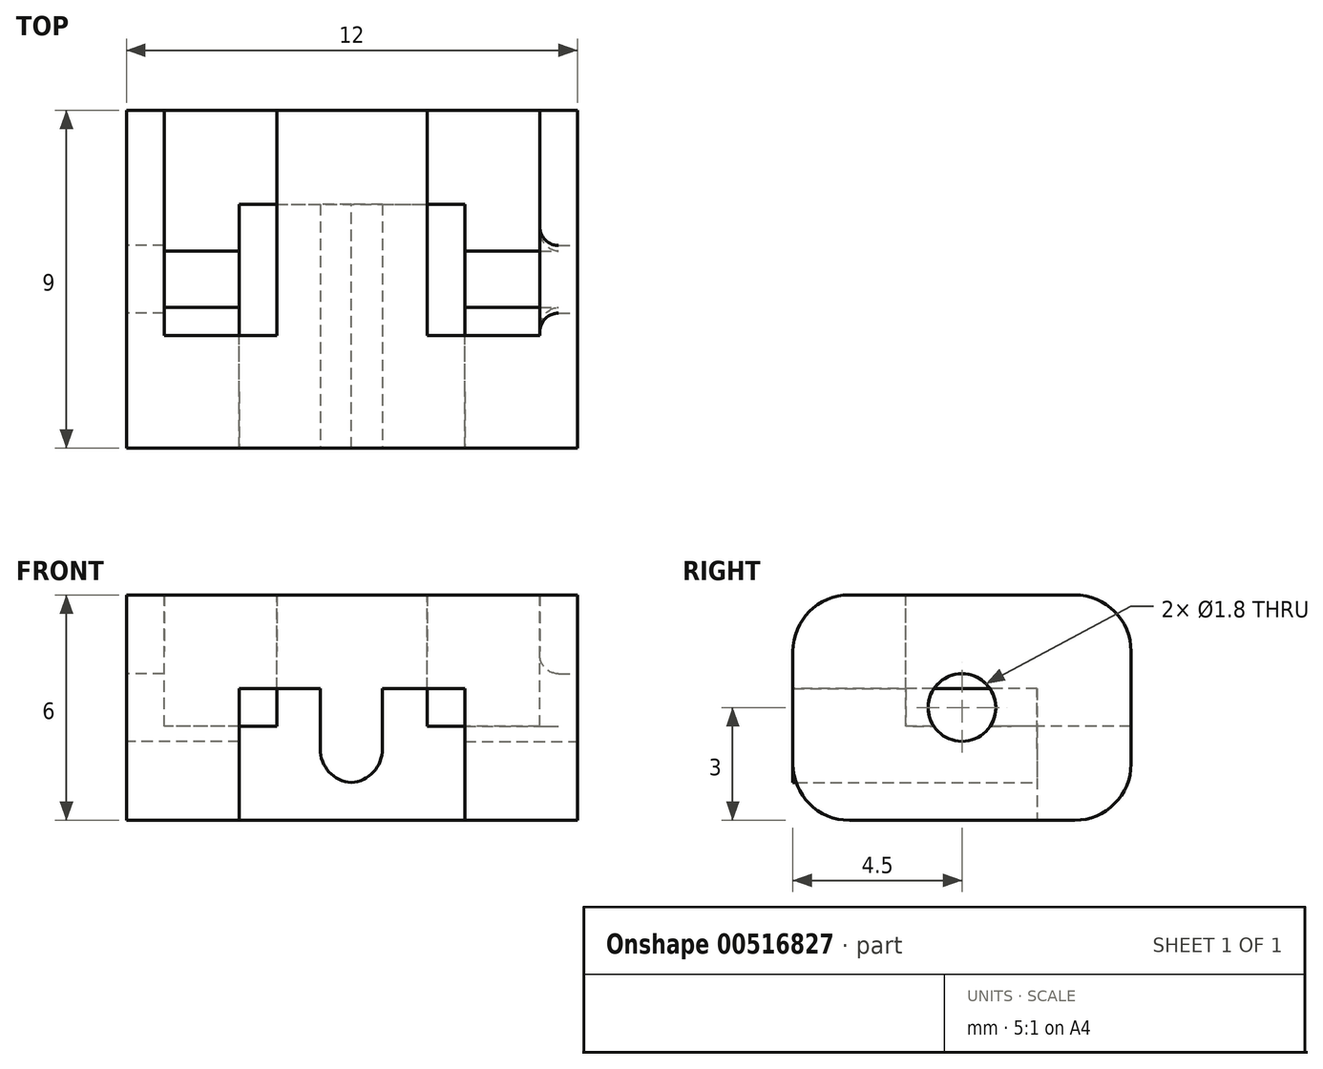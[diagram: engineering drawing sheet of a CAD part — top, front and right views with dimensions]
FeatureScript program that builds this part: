
annotation { "Feature Type Name" : "Feature", "Feature Type Description" : "" }
export const myFeature = defineFeature(function(context is Context, id is Id, definition is map)
    precondition{}
    {
        {
            var Q0;
            Q0=qCreatedBy(makeId("Top.planeOp"),FACE);
            var sketch = newSketch(context, id + "F0", { "sketchPlane" : qUnion([Q0])});
            skLineSegment(sketch, "E0.bottom", {"start": v(6, -4.5) * mm, "end": v(-6, -4.5) * mm});
            skLineSegment(sketch, "E0.top", {"start": v(6, 4.5) * mm, "end": v(-6, 4.5) * mm});
            skLineSegment(sketch, "E0.left", {"start": v(6, -4.5) * mm, "end": v(6, 4.5) * mm});
            skLineSegment(sketch, "E0.right", {"start": v(-6, -4.5) * mm, "end": v(-6, 4.5) * mm});
            skPoint(sketch, "E0.middle", {"position": v(0, 0) * mm});
            skSolve(sketch);
        }
        {
            var Q0;
            Q0=qSketchRegion(id+"F0",true);
            extrude(context, id + "F1", {"entities" : qUnion([Q0]), "depth" : 6 * mm, "offsetDistance" : 25 * mm});
        }
        {
            var Q0;
            Q0=makeQuery(id+"F1.opExtrude","CAP_FACE",FACE,{"disambiguationData":[OSD([sQuery(id+"F0.wireOp",EDGE,"E0.bottom"),sQuery(id+"F0.wireOp",EDGE,"E0.top"),sQuery(id+"F0.wireOp",EDGE,"E0.left"),sQuery(id+"F0.wireOp",EDGE,"E0.right")])],"isStart":false});
            var sketch = newSketch(context, id + "F2", { "sketchPlane" : qUnion([Q0])});
            skLineSegment(sketch, "E1.bottom", {"start": v(-5, 4.5) * mm, "end": v(-2, 4.5) * mm});
            skLineSegment(sketch, "E1.top", {"start": v(-5, -1.5) * mm, "end": v(-2, -1.5) * mm});
            skLineSegment(sketch, "E1.left", {"start": v(-5, 4.5) * mm, "end": v(-5, -1.5) * mm});
            skLineSegment(sketch, "E1.right", {"start": v(-2, 4.5) * mm, "end": v(-2, -1.5) * mm});
            skLineSegment(sketch, "E2.bottom", {"start": v(5, 4.5) * mm, "end": v(2, 4.5) * mm});
            skLineSegment(sketch, "E2.top", {"start": v(5, -1.5) * mm, "end": v(2, -1.5) * mm});
            skLineSegment(sketch, "E2.left", {"start": v(5, 4.5) * mm, "end": v(5, -1.5) * mm});
            skLineSegment(sketch, "E2.right", {"start": v(2, 4.5) * mm, "end": v(2, -1.5) * mm});
            skSolve(sketch);
        }
        {
            var Q0;
            Q0=makeQuery(id+"F2.imprint","IMPRINT",FACE,{"disambiguationData":[TD([[makeQuery(id+"F2.imprint","IMPRINT",EDGE,{"derivedFrom":sQuery(id+"F2.wireOp",EDGE,"E2.bottom")}),1.0]])]});
            var Q1;
            Q1=makeQuery(id+"F2.imprint","IMPRINT",FACE,{"disambiguationData":[TD([[makeQuery(id+"F2.imprint","IMPRINT",EDGE,{"derivedFrom":sQuery(id+"F2.wireOp",EDGE,"E1.bottom")}),1.0]])]});
            extrude(context, id + "F3", {"entities" : qUnion([Q0, Q1]), "operationType" : NewBodyOperationType.REMOVE, "oppositeDirection" : true, "depth" : 3.5 * mm, "offsetDistance" : 25 * mm});
        }
        {
            var Q0;
            Q0=makeQuery(id+"F1.opExtrude","CAP_FACE",FACE,{"disambiguationData":[OSD([sQuery(id+"F0.wireOp",EDGE,"E0.bottom"),sQuery(id+"F0.wireOp",EDGE,"E0.top"),sQuery(id+"F0.wireOp",EDGE,"E0.left"),sQuery(id+"F0.wireOp",EDGE,"E0.right")])],"isStart":true});
            var sketch = newSketch(context, id + "F4", { "sketchPlane" : qUnion([Q0])});
            skLineSegment(sketch, "E3.bottom", {"start": v(-3, 4.5) * mm, "end": v(3, 4.5) * mm});
            skLineSegment(sketch, "E3.top", {"start": v(-3, -2) * mm, "end": v(3, -2) * mm});
            skLineSegment(sketch, "E3.left", {"start": v(-3, 4.5) * mm, "end": v(-3, -2) * mm});
            skLineSegment(sketch, "E3.right", {"start": v(3, 4.5) * mm, "end": v(3, -2) * mm});
            skSolve(sketch);
        }
        {
            var Q0;
            Q0=qSketchRegion(id+"F4",true);
            extrude(context, id + "F5", {"entities" : qUnion([Q0]), "operationType" : NewBodyOperationType.REMOVE, "oppositeDirection" : true, "depth" : 3.5 * mm, "offsetDistance" : 25 * mm});
        }
        {
            var Q0;
            Q0=makeQuery(id+"F1.opExtrude","SWEPT_FACE",FACE,{"disambiguationData":[OSD([sQuery(id+"F0.wireOp",EDGE,"E0.left")])]});
            var sketch = newSketch(context, id + "F6", { "sketchPlane" : qUnion([Q0])});
            skLineSegment(sketch, "E4", {"start": v(0, 6) * mm, "end": v(0, 0) * mm, "construction": true});
            skLineSegment(sketch, "E5", {"start": v(-4.5, 3) * mm, "end": v(4.5, 3) * mm, "construction": true});
            skCircle(sketch, "E6", {"center": v(0, 3) * mm, "radius": 0.9 * mm});
            skSolve(sketch);
        }
        {
            var Q0;
            Q0=qSketchRegion(id+"F6",true);
            extrude(context, id + "F7", {"entities" : qUnion([Q0]), "operationType" : NewBodyOperationType.REMOVE, "oppositeDirection" : true, "depth" : 3 * mm, "offsetDistance" : 25 * mm});
        }
        {
            var Q0;
            Q0=makeQuery(id+"F1.opExtrude","SWEPT_FACE",FACE,{"disambiguationData":[OSD([sQuery(id+"F0.wireOp",EDGE,"E0.right")])]});
            var sketch = newSketch(context, id + "F8", { "sketchPlane" : qUnion([Q0])});
            skLineSegment(sketch, "E7", {"start": v(-4.5, 3) * mm, "end": v(4.5, 3) * mm, "construction": true});
            skLineSegment(sketch, "E8", {"start": v(0, 6) * mm, "end": v(0, 0) * mm, "construction": true});
            skCircle(sketch, "E9", {"center": v(0, 3) * mm, "radius": 0.9 * mm});
            skSolve(sketch);
        }
        {
            var Q0;
            Q0=qSketchRegion(id+"F8",true);
            extrude(context, id + "F9", {"entities" : qUnion([Q0]), "operationType" : NewBodyOperationType.REMOVE, "endBound" : BoundingType.UP_TO_NEXT, "oppositeDirection" : true, "depth" : 3 * mm, "offsetDistance" : 25 * mm});
        }
        {
            var Q0;
            Q0=makeQuery(id+"F3.boolean.opBoolean","COPY",EDGE,{"derivedFrom":makeQuery(id+"F3.opExtrude","CAP_EDGE",EDGE,{"disambiguationData":[OSD([sQuery(id+"F2.wireOp",EDGE,"E2.right")])],"isStart":true})});
            var Q1;
            Q1=makeQuery(id+"F3.boolean.opBoolean","COPY",EDGE,{"derivedFrom":makeQuery(id+"F3.opExtrude","CAP_EDGE",EDGE,{"disambiguationData":[OSD([sQuery(id+"F2.wireOp",EDGE,"E1.right")])],"isStart":true})});
            var Q2;
            Q2=makeQuery(id+"F1.opExtrude","CAP_EDGE",EDGE,{"disambiguationData":[OSD([sQuery(id+"F0.wireOp",EDGE,"E0.bottom")])],"isStart":false});
            var Q3;
            {var subQ0=sQuery(id+"F0.wireOp",EDGE,"E0.bottom");var subQ1=sQuery(id+"F0.wireOp",EDGE,"E0.right");Q3=makeQuery(id+"F5.boolean.opBoolean","SPLIT",EDGE,{"disambiguationData":[TD([makeQuery(id+"F1.opExtrude","SWEPT_FACE",FACE,{"disambiguationData":[OSD([subQ1])]})])],"derivedFrom":makeQuery(id+"F1.opExtrude","CAP_EDGE",EDGE,{"disambiguationData":[OSD([subQ0])],"isStart":true})});}
            var Q4;
            {var subQ0=sQuery(id+"F0.wireOp",EDGE,"E0.bottom");var subQ1=sQuery(id+"F0.wireOp",EDGE,"E0.left");Q4=makeQuery(id+"F5.boolean.opBoolean","SPLIT",EDGE,{"disambiguationData":[TD([makeQuery(id+"F1.opExtrude","SWEPT_FACE",FACE,{"disambiguationData":[OSD([subQ1])]})])],"derivedFrom":makeQuery(id+"F1.opExtrude","CAP_EDGE",EDGE,{"disambiguationData":[OSD([subQ0])],"isStart":true})});}
            var Q5;
            Q5=makeQuery(id+"F1.opExtrude","CAP_EDGE",EDGE,{"disambiguationData":[OSD([sQuery(id+"F0.wireOp",EDGE,"E0.top")])],"isStart":true});
            var Q6;
            {var subQ0=sQuery(id+"F0.wireOp",EDGE,"E0.right");var subQ1=sQuery(id+"F0.wireOp",EDGE,"E0.top");Q6=makeQuery(id+"F3.boolean.opBoolean","SPLIT",EDGE,{"disambiguationData":[TD([makeQuery(id+"F1.opExtrude","SWEPT_FACE",FACE,{"disambiguationData":[OSD([subQ0])]})])],"derivedFrom":makeQuery(id+"F1.opExtrude","CAP_EDGE",EDGE,{"disambiguationData":[OSD([subQ1])],"isStart":false})});}
            var Q7;
            {var subQ0=sQuery(id+"F0.wireOp",EDGE,"E0.left");var subQ1=sQuery(id+"F0.wireOp",EDGE,"E0.top");Q7=makeQuery(id+"F3.boolean.opBoolean","SPLIT",EDGE,{"disambiguationData":[TD([makeQuery(id+"F1.opExtrude","SWEPT_FACE",FACE,{"disambiguationData":[OSD([subQ0])]})])],"derivedFrom":makeQuery(id+"F1.opExtrude","CAP_EDGE",EDGE,{"disambiguationData":[OSD([subQ1])],"isStart":false})});}
            var Q8;
            {var subQ0=sQuery(id+"F0.wireOp",EDGE,"E0.top");Q8=makeQuery(id+"F3.boolean.opBoolean","SPLIT",EDGE,{"disambiguationData":[TD([makeQuery(id+"F3.opExtrude","SWEPT_FACE",FACE,{"disambiguationData":[OSD([sQuery(id+"F2.wireOp",EDGE,"E1.right")])]})])],"derivedFrom":makeQuery(id+"F1.opExtrude","CAP_EDGE",EDGE,{"disambiguationData":[OSD([subQ0])],"isStart":false})});}
            fillet(context, id + "F10", {"entities" : qUnion([Q0, Q1, Q2, Q3, Q4, Q5, Q6, Q7, Q8]), "radius" : 1.5 * mm, "tangentPropagation" : true, "allowEdgeOverflow" : false});
        }
        {
            var Q0;
            Q0=makeQuery(id+"F5.boolean.opBoolean","COPY",FACE,{"derivedFrom":makeQuery(id+"F5.opExtrude","CAP_FACE",FACE,{"disambiguationData":[OSD([sQuery(id+"F4.wireOp",EDGE,"E3.bottom"),sQuery(id+"F4.wireOp",EDGE,"E3.top"),sQuery(id+"F4.wireOp",EDGE,"E3.left"),sQuery(id+"F4.wireOp",EDGE,"E3.right")])],"isStart":false})});
            var sketch = newSketch(context, id + "F11", { "sketchPlane" : qUnion([Q0])});
            skLineSegment(sketch, "E10.bottom", {"start": v(0.81, -2) * mm, "end": v(-0.85, -2) * mm});
            skLineSegment(sketch, "E10.top", {"start": v(0.81, 4.5) * mm, "end": v(-0.85, 4.5) * mm});
            skLineSegment(sketch, "E10.left", {"start": v(0.81, -2) * mm, "end": v(0.81, 4.5) * mm});
            skLineSegment(sketch, "E10.right", {"start": v(-0.85, -2) * mm, "end": v(-0.85, 4.5) * mm});
            skSolve(sketch);
        }
        {
            var Q0;
            Q0=makeQuery(id+"F11.imprint","IMPRINT",FACE,{"disambiguationData":[TD([[makeQuery(id+"F11.imprint","IMPRINT",EDGE,{"derivedFrom":sQuery(id+"F11.wireOp",EDGE,"E10.bottom")}),1.0]])]});
            extrude(context, id + "F12", {"entities" : qUnion([Q0]), "operationType" : NewBodyOperationType.ADD, "depth" : 2.5 * mm, "offsetDistance" : 25 * mm});
        }
        {
            var Q0;
            Q0=makeQuery(id+"F12.opExtrude","CAP_EDGE",EDGE,{"disambiguationData":[OSD([sQuery(id+"F11.wireOp",EDGE,"E10.left")])],"isStart":false});
            var Q1;
            Q1=makeQuery(id+"F12.opExtrude","CAP_EDGE",EDGE,{"disambiguationData":[OSD([sQuery(id+"F11.wireOp",EDGE,"E10.right")])],"isStart":false});
            fillet(context, id + "F13", {"entities" : qUnion([Q0, Q1]), "radius" : 0.9 * mm, "tangentPropagation" : true, "allowEdgeOverflow" : false});
        }
        {
            var Q0;
            Q0=makeQuery(id+"F7.boolean.opBoolean","COPY",EDGE,{"derivedFrom":makeQuery(id+"F7.opExtrude","CAP_EDGE",EDGE,{"disambiguationData":[OSD([sQuery(id+"F6.wireOp",EDGE,"E6")])],"isStart":true})});
            var Q1;
            Q1=makeQuery(id+"F9.boolean.opBoolean","COPY",EDGE,{"derivedFrom":makeQuery(id+"F9.opExtrude","CAP_EDGE",EDGE,{"disambiguationData":[OSD([sQuery(id+"F8.wireOp",EDGE,"E9")])],"isStart":true})});
            var Q2;
            Q2=makeQuery(id+"F9.boolean.opBoolean","COPY",EDGE,{"derivedFrom":makeQuery(id+"F9.opExtrude","CAP_EDGE",EDGE,{"disambiguationData":[OSD([sQuery(id+"F8.wireOp",EDGE,"E9")]),topologyDisambiguationEdgeConnected([makeQuery(id+"F3.boolean.opBoolean","COPY",FACE,{"derivedFrom":makeQuery(id+"F3.opExtrude","SWEPT_FACE",FACE,{"disambiguationData":[OSD([sQuery(id+"F2.wireOp",EDGE,"E1.left")])]})})])],"isStart":false})});
            var Q3;
            Q3=makeQuery(id+"F7.boolean.opBoolean","INTERSECT",EDGE,{"derivedFrom":[makeQuery(id+"F3.boolean.opBoolean","COPY",FACE,{"derivedFrom":makeQuery(id+"F3.opExtrude","SWEPT_FACE",FACE,{"disambiguationData":[OSD([sQuery(id+"F2.wireOp",EDGE,"E2.left")])]})}),makeQuery(id+"F7.opExtrude","SWEPT_FACE",FACE,{"disambiguationData":[OSD([sQuery(id+"F6.wireOp",EDGE,"E6")])]})]});
            var Q4;
            Q4=makeQuery(id+"F9.boolean.opBoolean","COPY",EDGE,{"derivedFrom":makeQuery(id+"F9.opExtrude","CAP_EDGE",EDGE,{"disambiguationData":[OSD([sQuery(id+"F8.wireOp",EDGE,"E9")]),topologyDisambiguationEdgeConnected([makeQuery(id+"F5.boolean.opBoolean","COPY",FACE,{"derivedFrom":makeQuery(id+"F5.opExtrude","SWEPT_FACE",FACE,{"disambiguationData":[OSD([sQuery(id+"F4.wireOp",EDGE,"E3.left")])]})})])],"isStart":false})});
            var Q5;
            Q5=makeQuery(id+"F7.boolean.opBoolean","COPY",EDGE,{"derivedFrom":makeQuery(id+"F7.opExtrude","CAP_EDGE",EDGE,{"disambiguationData":[OSD([sQuery(id+"F6.wireOp",EDGE,"E6")])],"isStart":false})});
            fillet(context, id + "F14", {"entities" : qUnion([Q0, Q1, Q2, Q3, Q4, Q5]), "radius" : .5 * mm, "tangentPropagation" : true, "allowEdgeOverflow" : false});
        }
    });
